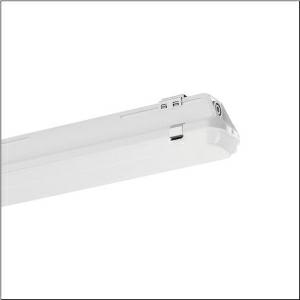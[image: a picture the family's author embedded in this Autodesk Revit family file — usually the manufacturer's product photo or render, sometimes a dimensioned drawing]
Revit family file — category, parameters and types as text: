
# Revit family: monsun_r__11_51fp209p460h_6055
name_source: partatom
category: Lighting Fixtures
units: mm (PartAtom-declared; Revit-internal decimal feet)

## family parameters
Cut with Voids When Loaded = No
Host = Face
Light Source = No
Part Type = Normal
Room Calculation Point = No
Round Connector Dimension = Use Diameter
Shared = No

## types (1)
- Monsun® 11 (1 x LED, 5490 lm, 34 W, 4000K)
    Apparent Load = 34 VA
    CIE Flux Codes = 45 75 93 94 100
    Color Rendering = 80
    Color Temperature = 4000K
    Default Elevation = 1800 mm
    Description = Monsun® 11, damp-proof luminaire, chain hanger, primary optical cover: enclosure, of PC, light emission: direct distribution, primary light characteristic: symmetric, installation type: suspended mounting, surface-mounted, horizontal mounting, vertical mounting, LED, rated luminous flux: 5.490lm, luminous efficacy: 161lm/W, light colour: 840, colour temperature: 4000K, control gear: ON/OFF, with terminal, 3-pole, max. 2.5mm², mains connection: 220..240V, AC, 50/60Hz, rated input power: 34W, luminaire housing, of glass-fibre reinforced polyester, uncoated, bright grey, incl. chain hanger, length: 1.590mm, width: 90mm, height: 88mm, clip for enclosure, of stainless steel (V2A), ceiling mounting element, of stainless steel (V2A), chain hanger, of stainless steel (V2A), protection rating (complete): IP66, insulation class (complete): insulation class I (protective earthing), certification: CE, ENEC, VDE, UKCA, protection symbol: D, impact resistance: IK08, permissible operating ambient temperature: -35..+40°C, standard: EN 50419, EN 60598-2-1, no direct snow, no direct sun, no direct rain, for indoor or canopied outdoor use, corresponds to IFS (International Featured Standards) requirements for safety and quality in the food industry, contact your sales advisor before using the luminaires in applications with unclear chemical exposure, large temperature fluctuations or condensation-forming humidity, LABS conformity tested according to VDMA 24364:2018-05, packaging unit: 1 piece
    Height = 89 mm
    Lamp = 1 x LED
    Lamp Light Flux = 5490 lm
    Lamp Power = 34 W
    Lamp count = 1
    Length = 1590 mm
    Luminous efficacy = 161 lm/W
    Manufacturer = Siteco
    ModVariant = No
    Model = 51FP209P460H
    Mounting Place = Ceiling
    Mounting Type = Surface mounted
    Number of Poles = 1
    OnlyDefault = Yes
    Power Factor = 1
    Product Name = Monsun® 11
    Product group = damp-proof luminaire
    ProductGroupID = 300
    Protection Class = Protection class I
    Protection Degree = IP 66
    RLX_Detail_Level = 1
    RLX_Emergency_Light_Flux = 0 lm
    RLX_Emergency_Type = 0
    RLX_Emergency_Type_DB = No
    RlxData = <blob elided: 88601 chars, md5=33d9a3f1>
    Socket = socket
    Standby Power = 0 W
    System Light Flux = 5490 lm
    System Power = 34 W
    Type Comments = Product without accessories
    Type Image = l_1349237.jpg
    URL = http://relux.com
    VarID = ---
    Voltage = 0 V
    Weight = 0.00 kg
    Width = 90 mm

## geometry (parser evidence)
native form markers: Blend x4, Sweep x12
no freeform markers — native parametric forms only
